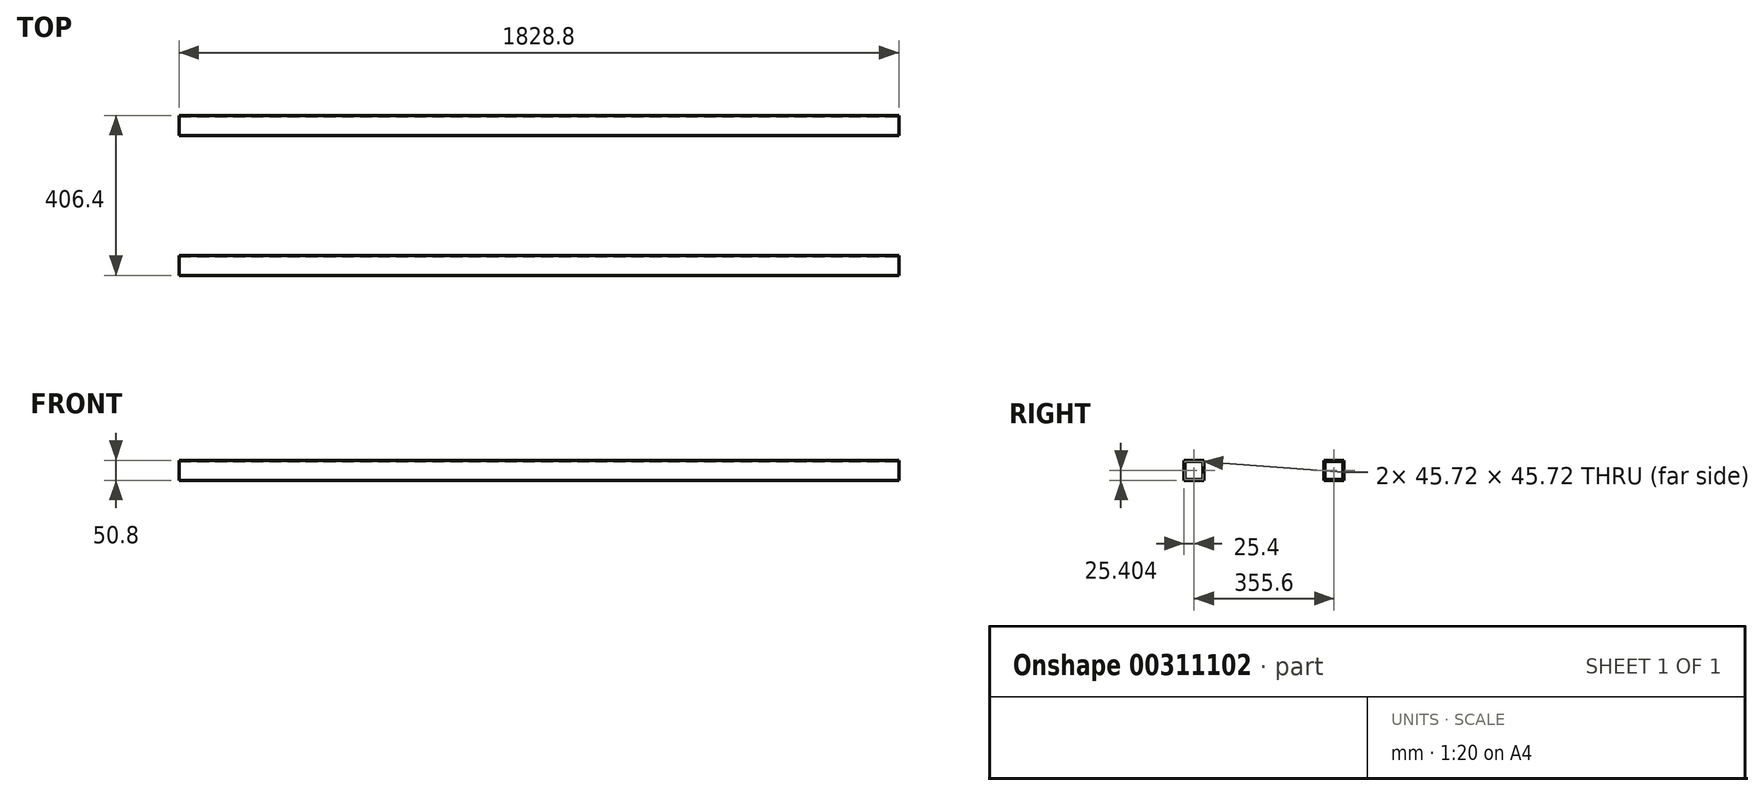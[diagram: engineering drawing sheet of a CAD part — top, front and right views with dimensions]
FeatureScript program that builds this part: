
annotation { "Feature Type Name" : "Feature", "Feature Type Description" : "" }
export const myFeature = defineFeature(function(context is Context, id is Id, definition is map)
    precondition{}
    {
        {
            var Q0;
            Q0=qCreatedBy(makeId("Front.planeOp"),FACE);
            var sketch = newSketch(context, id + "F0", { "sketchPlane" : qUnion([Q0])});
            skLineSegment(sketch, "E0.bottom", {"start": v(-1781.6, 96.9) * mm, "end": v(47.2, 96.9) * mm});
            skLineSegment(sketch, "E0.top", {"start": v(-1781.6, 46.1) * mm, "end": v(47.2, 46.1) * mm});
            skLineSegment(sketch, "E0.left", {"start": v(-1781.6, 96.9) * mm, "end": v(-1781.6, 46.1) * mm});
            skLineSegment(sketch, "E0.right", {"start": v(47.2, 96.9) * mm, "end": v(47.2, 46.1) * mm});
            skSolve(sketch);
        }
        {
            var Q0;
            Q0 = qSketchRegion(id + "F0", true);
            extrude(context, id + "F1", {"entities" : qUnion([Q0]), "depth" : 50.8 * mm});
        }
        {
            var Q0;
            Q0=makeQuery(id+"F1.opExtrude","SWEPT_FACE",FACE,{"disambiguationData":[OSD([sQuery(id+"F0.wireOp",EDGE,"E0.right")])]});
            var Q1;
            Q1=makeQuery(id+"F1.opExtrude","SWEPT_FACE",FACE,{"disambiguationData":[OSD([sQuery(id+"F0.wireOp",EDGE,"E0.left")])]});
            shell(context, id + "F2", {"entities" : qUnion([Q0, Q1]), "thickness" : 2.54 * mm});
        }
        {
            var Q0;
            Q0=makeQuery(id+"F1.opExtrude","SWEPT_BODY",BODY,{"disambiguationData":[OSD([sQuery(id+"F0.wireOp",EDGE,"E0.bottom"),sQuery(id+"F0.wireOp",EDGE,"E0.top"),sQuery(id+"F0.wireOp",EDGE,"E0.left"),sQuery(id+"F0.wireOp",EDGE,"E0.right")])]});
            transform(context, id + "F3", {"entities" : qUnion([Q0]), "transformType" : TransformType.TRANSLATION_3D, "dx" : 0 * mm, "dy" : 355.6 * mm, "dz" : 0 * mm, "makeCopy" : true});
        }
    });
